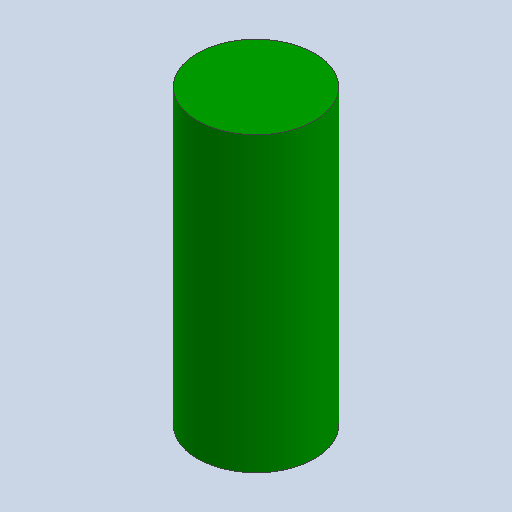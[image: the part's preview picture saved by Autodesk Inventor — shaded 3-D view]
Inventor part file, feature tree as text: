
AUTODESK INVENTOR PART (.ipt)
format: ipt  version: 2025.2 (Build 292293000, 293)  size: 90,624 bytes
history: native  units: in
note: dims shown in document units (in); Inventor stores cm internally (conversion verified against a paired STEP export)
features: other x3, sketch x1
ambient origin geometry x8: Origin, YZ Plane, XZ Plane, XY Plane, X Axis, Y Axis, Z Axis, Center Point
bodies: Solid1 (feature_tree)
feature tree (4):
  other  "26650(Green)_MIR3.ipt"
  other  "Solid1::26650(Green)_MIR3.ipt"
  other  "TaggingFeature1"
  sketch  "Sketch1"  dims[d0=0.3937in]
